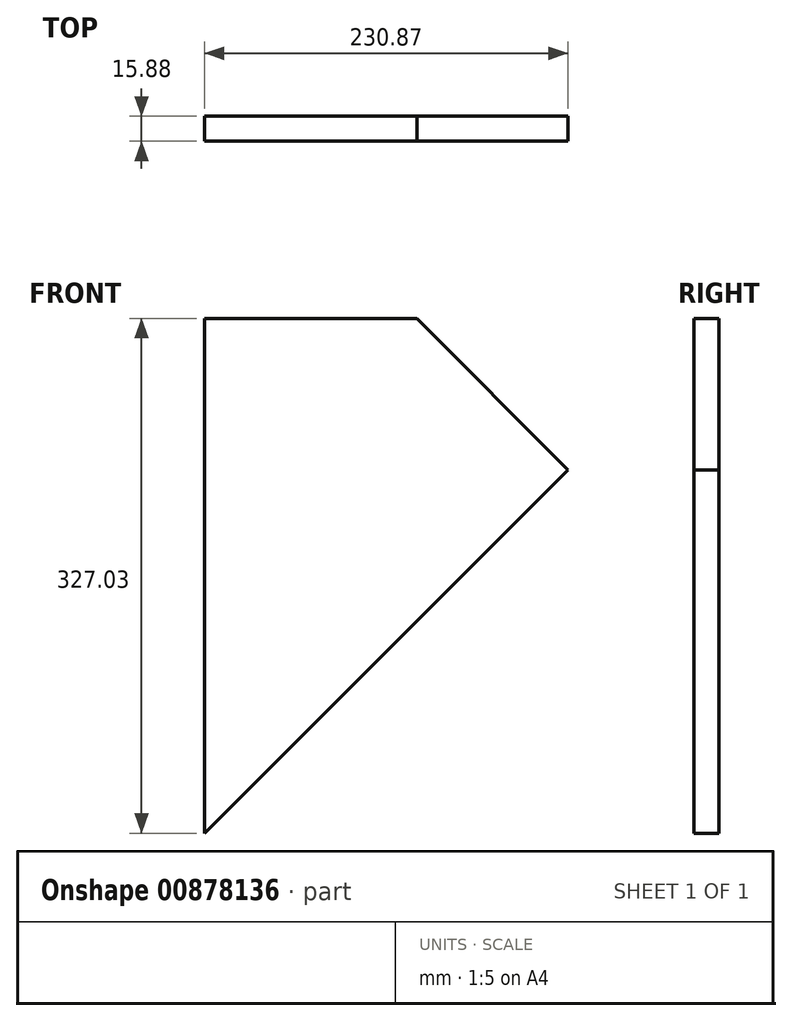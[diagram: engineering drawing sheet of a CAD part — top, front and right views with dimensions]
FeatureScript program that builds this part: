
annotation { "Feature Type Name" : "Feature", "Feature Type Description" : "" }
export const myFeature = defineFeature(function(context is Context, id is Id, definition is map)
    precondition{}
    {
        {
            var Q0;
            Q0=qCreatedBy(makeId("Front.planeOp"),FACE);
            var sketch = newSketch(context, id + "F0", { "sketchPlane" : qUnion([Q0])});
            skLineSegment(sketch, "E0", {"start": v(0, 0) * mm, "end": v(0, 327.03) * mm});
            skLineSegment(sketch, "E1", {"start": v(0, 327.03) * mm, "end": v(134.92, 327.03) * mm});
            skLineSegment(sketch, "E2", {"start": v(134.92, 327.03) * mm, "end": v(230.87, 230.78) * mm});
            skLineSegment(sketch, "E3", {"start": v(230.87, 230.78) * mm, "end": v(0, 0) * mm});
            skSolve(sketch);
        }
        {
            var Q0;
            Q0 = qSketchRegion(id + "F0", true);
            extrude(context, id + "F1", {"entities" : qUnion([Q0]), "depth" : 15.88 * mm, "offsetDistance" : 25.4 * mm});
        }
    });
